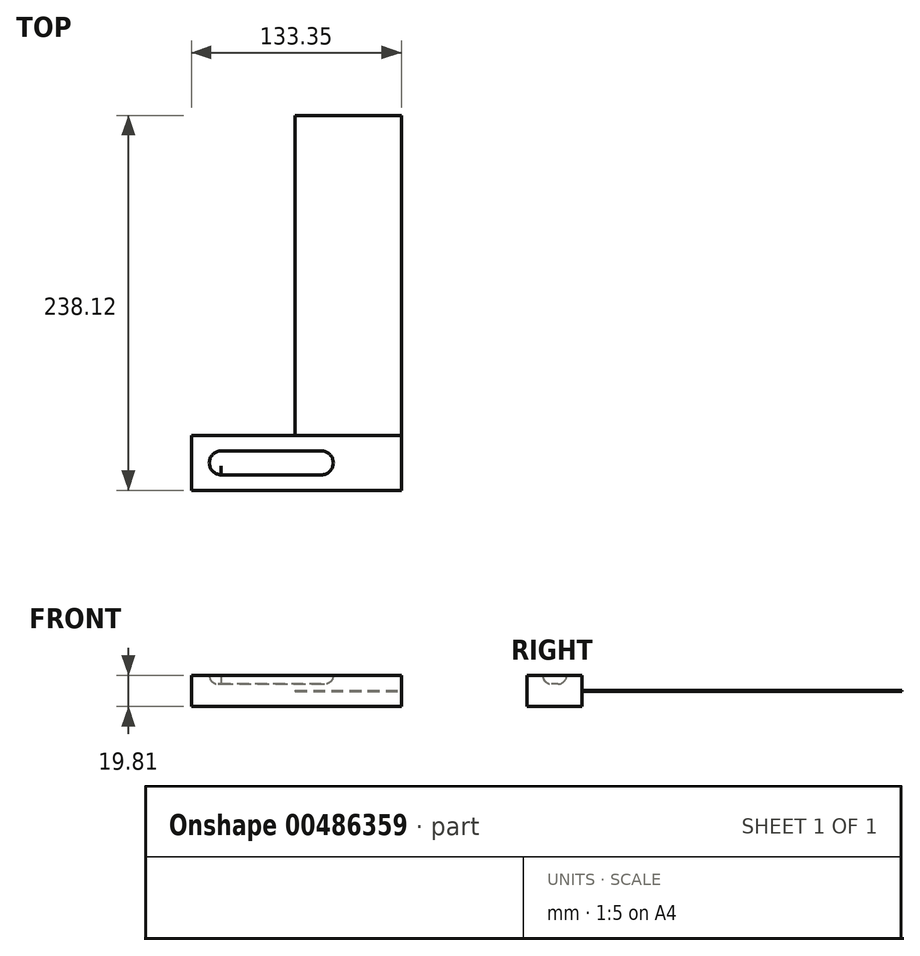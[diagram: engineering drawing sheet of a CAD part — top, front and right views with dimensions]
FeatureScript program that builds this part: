
annotation { "Feature Type Name" : "Feature", "Feature Type Description" : "" }
export const myFeature = defineFeature(function(context is Context, id is Id, definition is map)
    precondition{}
    {
        {
            var Q0;
            Q0=qCreatedBy(makeId("Top.planeOp"),FACE);
            var sketch = newSketch(context, id + "F0", { "sketchPlane" : qUnion([Q0])});
            skLineSegment(sketch, "E0.bottom", {"start": v(-66.02, 60.68) * mm, "end": v(67.33, 60.68) * mm});
            skLineSegment(sketch, "E0.top", {"start": v(-66.02, 25.76) * mm, "end": v(67.33, 25.76) * mm});
            skLineSegment(sketch, "E0.left", {"start": v(-66.02, 60.68) * mm, "end": v(-66.02, 25.76) * mm});
            skLineSegment(sketch, "E0.right", {"start": v(67.33, 60.68) * mm, "end": v(67.33, 25.76) * mm});
            skSolve(sketch);
        }
        {
            var Q0;
            Q0 = qSketchRegion(id + "F0", true);
            extrude(context, id + "F1", {"entities" : qUnion([Q0]), "depth" : 19.8 * mm});
        }
        {
            var Q0;
            Q0=makeQuery(id+"F1.opExtrude","CAP_FACE",FACE,{"disambiguationData":[OSD([sQuery(id+"F0.wireOp",EDGE,"E0.bottom"),sQuery(id+"F0.wireOp",EDGE,"E0.top"),sQuery(id+"F0.wireOp",EDGE,"E0.left"),sQuery(id+"F0.wireOp",EDGE,"E0.right")])],"isStart":false});
            var sketch = newSketch(context, id + "F2", { "sketchPlane" : qUnion([Q0])});
            skLineSegment(sketch, "E1", {"start": v(16.53, 50.84) * mm, "end": v(-46.97, 50.84) * mm});
            skArc(sketch, "E2", {"start": v(-46.97, 50.84) * mm, "mid": v(-54.59, 43.28) * mm, "end": v(-47.08, 35.6) * mm});
            skLineSegment(sketch, "E3", {"start": v(-47.08, 35.6) * mm, "end": v(16.53, 35.6) * mm});
            skArc(sketch, "E4", {"start": v(16.53, 35.6) * mm, "mid": v(24.15, 43.22) * mm, "end": v(16.53, 50.84) * mm});
            skSolve(sketch);
        }
        {
            var Q0;
            Q0 = qSketchRegion(id + "F2", true);
            extrude(context, id + "F3", {"entities" : qUnion([Q0]), "operationType" : NewBodyOperationType.REMOVE, "oppositeDirection" : true, "depth" : 5.6 * mm});
        }
        {
            var Q0;
            Q0=makeQuery(id+"F1.opExtrude","SWEPT_FACE",FACE,{"disambiguationData":[OSD([sQuery(id+"F0.wireOp",EDGE,"E0.bottom")])]});
            var sketch = newSketch(context, id + "F4", { "sketchPlane" : qUnion([Q0])});
            skLineSegment(sketch, "E5", {"start": v(-47.55, -47.13) * mm, "end": v(-70.98, -47.13) * mm});
            skPoint(sketch, "E6.end.orphan", {"position": v(0, 9.9) * mm});
            skPoint(sketch, "E6.start.orphan", {"position": v(-67.33, 9.9) * mm});
            skPoint(sketch, "E7.start.orphan", {"position": v(0, 13.05) * mm});
            skLineSegment(sketch, "E8", {"start": v(0, 9.9) * mm, "end": v(0, 10.16) * mm});
            skLineSegment(sketch, "E9", {"start": v(0, 10.16) * mm, "end": v(0, 9.9) * mm});
            skLineSegment(sketch, "E10", {"start": v(0, 9.9) * mm, "end": v(0, 9.65) * mm});
            skLineSegment(sketch, "E11", {"start": v(0, 9.65) * mm, "end": v(0, 9.9) * mm});
            skLineSegment(sketch, "E12.bottom", {"start": v(0, 9.65) * mm, "end": v(-67.33, 9.65) * mm});
            skLineSegment(sketch, "E12.top", {"start": v(0, 10.16) * mm, "end": v(-67.33, 10.16) * mm});
            skLineSegment(sketch, "E12.left", {"start": v(0, 9.65) * mm, "end": v(0, 10.16) * mm});
            skLineSegment(sketch, "E12.right", {"start": v(-67.33, 9.65) * mm, "end": v(-67.33, 10.16) * mm});
            skPoint(sketch, "E12.middle", {"position": v(-33.67, 9.9) * mm});
            skSolve(sketch);
        }
        {
            var Q0;
            Q0 = qSketchRegion(id + "F4", true);
            extrude(context, id + "F5", {"entities" : qUnion([Q0]), "depth" : 203.2 * mm});
        }
        {
            var Q0;
            Q0=makeQuery(id+"F3.boolean.opBoolean","COPY",FACE,{"derivedFrom":makeQuery(id+"F3.opExtrude","CAP_FACE",FACE,{"disambiguationData":[OSD([sQuery(id+"F2.wireOp",EDGE,"E1"),sQuery(id+"F2.wireOp",EDGE,"E2"),sQuery(id+"F2.wireOp",EDGE,"E3"),sQuery(id+"F2.wireOp",EDGE,"E4")])],"isStart":false})});
            fillet(context, id + "F6", {"entities" : qUnion([Q0]), "radius" : 5.6 * mm, "tangentPropagation" : true, "allowEdgeOverflow" : false});
        }
    });
